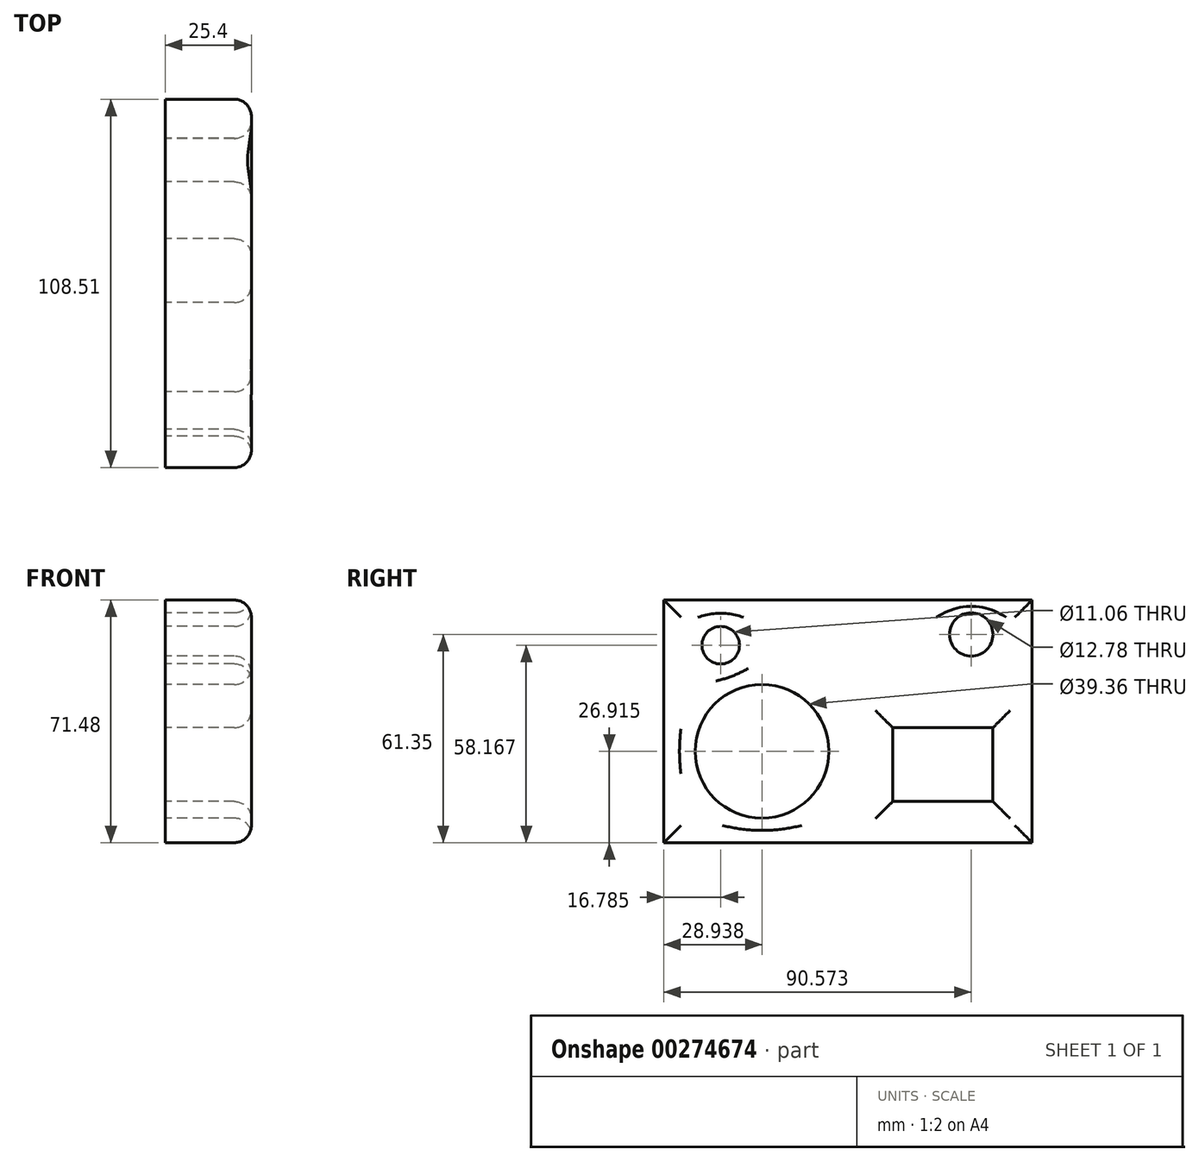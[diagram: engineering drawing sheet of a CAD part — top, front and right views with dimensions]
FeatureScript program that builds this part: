
annotation { "Feature Type Name" : "Feature", "Feature Type Description" : "" }
export const myFeature = defineFeature(function(context is Context, id is Id, definition is map)
    precondition{}
    {
        {
            var Q0;
            Q0=qCreatedBy(makeId("Right.planeOp"),FACE);
            var sketch = newSketch(context, id + "F0", { "sketchPlane" : qUnion([Q0])});
            skLineSegment(sketch, "E0.bottom", {"start": v(-55.56, 35.45) * mm, "end": v(52.95, 35.45) * mm});
            skLineSegment(sketch, "E0.top", {"start": v(-55.56, -36.03) * mm, "end": v(52.95, -36.03) * mm});
            skLineSegment(sketch, "E0.left", {"start": v(-55.56, 35.45) * mm, "end": v(-55.56, -36.03) * mm});
            skLineSegment(sketch, "E0.right", {"start": v(52.95, 35.45) * mm, "end": v(52.95, -36.03) * mm});
            skCircle(sketch, "E1", {"center": v(-38.78, 22.14) * mm, "radius": 5.53 * mm});
            skCircle(sketch, "E2", {"center": v(35.01, 25.32) * mm, "radius": 6.4 * mm});
            skCircle(sketch, "E3", {"center": v(-26.62, -9.12) * mm, "radius": 19.68 * mm});
            skLineSegment(sketch, "E4.bottom", {"start": v(11.86, -2.17) * mm, "end": v(41.38, -2.17) * mm});
            skLineSegment(sketch, "E4.top", {"start": v(11.86, -23.87) * mm, "end": v(41.38, -23.87) * mm});
            skLineSegment(sketch, "E4.left", {"start": v(11.86, -2.17) * mm, "end": v(11.86, -23.87) * mm});
            skLineSegment(sketch, "E4.right", {"start": v(41.38, -2.17) * mm, "end": v(41.38, -23.87) * mm});
            skSolve(sketch);
        }
        {
            var Q0;
            Q0 = qSketchRegion(id + "F0", true);
            extrude(context, id + "F1", {"entities" : qUnion([Q0]), "depth" : 25.4 * mm});
        }
        {
            var Q0;
            Q0=makeQuery(id+"F1.opExtrude","CAP_EDGE",EDGE,{"disambiguationData":[OSD([sQuery(id+"F0.wireOp",EDGE,"E4.bottom")])],"isStart":false});
            var Q1;
            Q1=makeQuery(id+"F1.opExtrude","CAP_FACE",FACE,{"disambiguationData":[OSD([sQuery(id+"F0.wireOp",EDGE,"E0.bottom"),sQuery(id+"F0.wireOp",EDGE,"E0.top"),sQuery(id+"F0.wireOp",EDGE,"E0.left"),sQuery(id+"F0.wireOp",EDGE,"E0.right"),sQuery(id+"F0.wireOp",EDGE,"E1"),sQuery(id+"F0.wireOp",EDGE,"E2"),sQuery(id+"F0.wireOp",EDGE,"E3"),sQuery(id+"F0.wireOp",EDGE,"E4.bottom"),sQuery(id+"F0.wireOp",EDGE,"E4.top"),sQuery(id+"F0.wireOp",EDGE,"E4.left"),sQuery(id+"F0.wireOp",EDGE,"E4.right")])],"isStart":false});
            fillet(context, id + "F2", {"entities" : qUnion([Q0, Q1]), "radius" : 5.08 * mm, "tangentPropagation" : true, "allowEdgeOverflow" : false});
        }
    });
